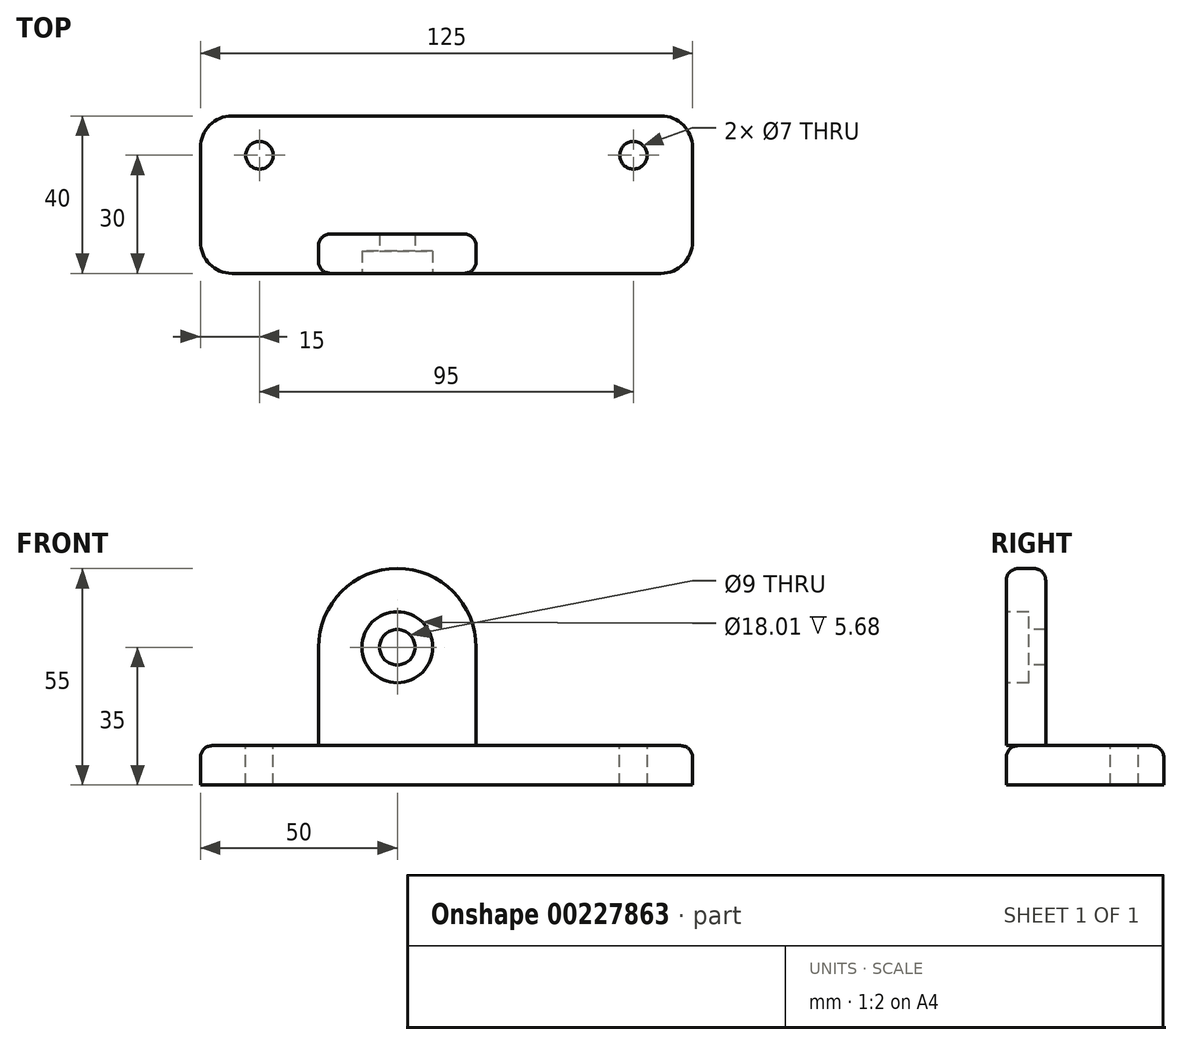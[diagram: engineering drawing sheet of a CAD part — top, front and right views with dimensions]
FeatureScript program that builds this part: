
annotation { "Feature Type Name" : "Feature", "Feature Type Description" : "" }
export const myFeature = defineFeature(function(context is Context, id is Id, definition is map)
    precondition{}
    {
        {
            var Q0;
            Q0=qCreatedBy(makeId("Top.planeOp"),FACE);
            var sketch = newSketch(context, id + "F0", { "sketchPlane" : qUnion([Q0])});
            skLineSegment(sketch, "E0.bottom", {"start": v(-62.5, 20) * mm, "end": v(62.5, 20) * mm});
            skLineSegment(sketch, "E0.top", {"start": v(-62.5, -20) * mm, "end": v(62.5, -20) * mm});
            skLineSegment(sketch, "E0.left", {"start": v(-62.5, 20) * mm, "end": v(-62.5, -20) * mm});
            skLineSegment(sketch, "E0.right", {"start": v(62.5, 20) * mm, "end": v(62.5, -20) * mm});
            skPoint(sketch, "E0.middle", {"position": v(0, 0) * mm});
            skSolve(sketch);
        }
        {
            var Q0;
            Q0=makeQuery(id+"F0.imprint","IMPRINT",FACE,{"disambiguationData":[TD([[makeQuery(id+"F0.imprint","IMPRINT",EDGE,{"derivedFrom":sQuery(id+"F0.wireOp",EDGE,"E0.bottom")}),-1.0]])]});
            extrude(context, id + "F1", {"entities" : qUnion([Q0]), "depth" : 10 * mm});
        }
        {
            var Q0;
            Q0=makeQuery(id+"F1.opExtrude","SWEPT_FACE",FACE,{"disambiguationData":[OSD([sQuery(id+"F0.wireOp",EDGE,"E0.top")])]});
            var sketch = newSketch(context, id + "F2", { "sketchPlane" : qUnion([Q0])});
            skLineSegment(sketch, "E1", {"start": v(-32.5, 10) * mm, "end": v(-32.5, 35) * mm});
            skLineSegment(sketch, "E2", {"start": v(7.5, 10) * mm, "end": v(7.5, 35) * mm});
            skArc(sketch, "E3", {"start": v(7.5, 35) * mm, "mid": v(-12.5, 55) * mm, "end": v(-32.5, 35) * mm});
            skSolve(sketch);
        }
        {
            var Q0;
            {var subQ0=sQuery(id+"F2.wireOp",EDGE,"E1");Q0=makeQuery(id+"F2.imprint","IMPRINT",FACE,{"disambiguationData":[TD([[makeQuery(id+"F2.imprint","IMPRINT",EDGE,{"derivedFrom":subQ0}),-1.0]])]});}
            extrude(context, id + "F3", {"entities" : qUnion([Q0]), "oppositeDirection" : true, "depth" : 10 * mm});
        }
        {
            var Q0;
            Q0=makeQuery(id+"F3.opExtrude","CAP_FACE",FACE,{"disambiguationData":[OSD([sQuery(id+"F0.wireOp",EDGE,"E0.top"),sQuery(id+"F2.wireOp",EDGE,"E1"),sQuery(id+"F2.wireOp",EDGE,"E2"),sQuery(id+"F2.wireOp",EDGE,"E3")])],"isStart":true});
            var sketch = newSketch(context, id + "F4", { "sketchPlane" : qUnion([Q0])});
            skPoint(sketch, "E4", {"position": v(-12.5, 35) * mm});
            skSolve(sketch);
        }
        {
            var Q0;
            Q0=sQuery(id+"F4.wireOp",VERTEX,"E4");
            var Q1;
            Q1=makeQuery(id+"F3.opExtrude","SWEPT_BODY",BODY,{"disambiguationData":[OSD([sQuery(id+"F0.wireOp",EDGE,"E0.top"),sQuery(id+"F2.wireOp",EDGE,"E1"),sQuery(id+"F2.wireOp",EDGE,"E2"),sQuery(id+"F2.wireOp",EDGE,"E3")])]});
            hole(context, id + "F5", {"style" : HoleStyle.C_BORE, "endStyle" : HoleEndStyle.THROUGH, "holeDiameter" : 9 * mm, "cBoreDiameter" : 18.01 * mm, "cBoreDepth" : 5.68 * mm, "locations" : qUnion([Q0]), "scope" : qUnion([Q1]), "isTappedThrough" : true});
        }
        {
            var Q0;
            Q0=makeQuery(id+"F1.opExtrude","CAP_FACE",FACE,{"disambiguationData":[OSD([sQuery(id+"F0.wireOp",EDGE,"E0.bottom"),sQuery(id+"F0.wireOp",EDGE,"E0.top"),sQuery(id+"F0.wireOp",EDGE,"E0.left"),sQuery(id+"F0.wireOp",EDGE,"E0.right")])],"isStart":false});
            var sketch = newSketch(context, id + "F6", { "sketchPlane" : qUnion([Q0])});
            skPoint(sketch, "E5", {"position": v(47.5, 10) * mm});
            skSolve(sketch);
        }
        {
            var Q0;
            Q0=sQuery(id+"F6.wireOp",VERTEX,"E5");
            var Q1;
            Q1=makeQuery(id+"F1.opExtrude","SWEPT_BODY",BODY,{"disambiguationData":[OSD([sQuery(id+"F0.wireOp",EDGE,"E0.bottom"),sQuery(id+"F0.wireOp",EDGE,"E0.top"),sQuery(id+"F0.wireOp",EDGE,"E0.left"),sQuery(id+"F0.wireOp",EDGE,"E0.right")])]});
            hole(context, id + "F7", {"style" : HoleStyle.SIMPLE, "endStyle" : HoleEndStyle.THROUGH, "holeDiameter" : 7 * mm, "locations" : qUnion([Q0]), "scope" : qUnion([Q1]), "isTappedThrough" : true});
        }
        {
            var Q0;
            Q0=makeQuery(id+"F1.opExtrude","CAP_FACE",FACE,{"disambiguationData":[OSD([sQuery(id+"F0.wireOp",EDGE,"E0.bottom"),sQuery(id+"F0.wireOp",EDGE,"E0.top"),sQuery(id+"F0.wireOp",EDGE,"E0.left"),sQuery(id+"F0.wireOp",EDGE,"E0.right")])],"isStart":false});
            var sketch = newSketch(context, id + "F8", { "sketchPlane" : qUnion([Q0])});
            skPoint(sketch, "E6", {"position": v(-47.5, 10) * mm});
            skSolve(sketch);
        }
        {
            var Q0;
            Q0=sQuery(id+"F8.wireOp",VERTEX,"E6");
            var Q1;
            Q1=makeQuery(id+"F1.opExtrude","SWEPT_BODY",BODY,{"disambiguationData":[OSD([sQuery(id+"F0.wireOp",EDGE,"E0.bottom"),sQuery(id+"F0.wireOp",EDGE,"E0.top"),sQuery(id+"F0.wireOp",EDGE,"E0.left"),sQuery(id+"F0.wireOp",EDGE,"E0.right")])]});
            hole(context, id + "F9", {"style" : HoleStyle.SIMPLE, "endStyle" : HoleEndStyle.THROUGH, "holeDiameter" : 7 * mm, "locations" : qUnion([Q0]), "scope" : qUnion([Q1]), "isTappedThrough" : true});
        }
        {
            var Q0;
            Q0=makeQuery(id+"F3.opExtrude","CAP_EDGE",EDGE,{"disambiguationData":[OSD([sQuery(id+"F2.wireOp",EDGE,"E3")])],"isStart":true});
            fillet(context, id + "F10", {"entities" : qUnion([Q0]), "radius" : 3 * mm, "tangentPropagation" : true, "allowEdgeOverflow" : false});
        }
        {
            var Q0;
            Q0=makeQuery(id+"F3.opExtrude","CAP_EDGE",EDGE,{"disambiguationData":[OSD([sQuery(id+"F2.wireOp",EDGE,"E3")])],"isStart":false});
            fillet(context, id + "F11", {"entities" : qUnion([Q0]), "radius" : 3 * mm, "tangentPropagation" : true, "allowEdgeOverflow" : false});
        }
        {
            var Q0;
            Q0=makeQuery(id+"F1.opExtrude","CAP_EDGE",EDGE,{"disambiguationData":[OSD([sQuery(id+"F0.wireOp",EDGE,"E0.left")])],"isStart":false});
            var Q1;
            Q1=makeQuery(id+"F1.opExtrude","CAP_EDGE",EDGE,{"disambiguationData":[OSD([sQuery(id+"F0.wireOp",EDGE,"E0.bottom")])],"isStart":false});
            var Q2;
            Q2=makeQuery(id+"F1.opExtrude","CAP_EDGE",EDGE,{"disambiguationData":[OSD([sQuery(id+"F0.wireOp",EDGE,"E0.right")])],"isStart":false});
            var Q3;
            Q3=makeQuery(id+"F1.opExtrude","CAP_EDGE",EDGE,{"disambiguationData":[OSD([sQuery(id+"F0.wireOp",EDGE,"E0.top")])],"isStart":false});
            fillet(context, id + "F12", {"entities" : qUnion([Q0, Q1, Q2, Q3]), "radius" : 3 * mm, "tangentPropagation" : true, "allowEdgeOverflow" : false});
        }
        {
            var Q0;
            Q0=makeQuery(id+"F1.opExtrude","SWEPT_EDGE",EDGE,{"disambiguationData":[OSD([sQuery(id+"F0.wireOp",EDGE,"E0.top"),sQuery(id+"F0.wireOp",EDGE,"E0.right")])]});
            var Q1;
            Q1=makeQuery(id+"F1.opExtrude","SWEPT_EDGE",EDGE,{"disambiguationData":[OSD([sQuery(id+"F0.wireOp",EDGE,"E0.bottom"),sQuery(id+"F0.wireOp",EDGE,"E0.right")])]});
            var Q2;
            Q2=makeQuery(id+"F1.opExtrude","SWEPT_EDGE",EDGE,{"disambiguationData":[OSD([sQuery(id+"F0.wireOp",EDGE,"E0.top"),sQuery(id+"F0.wireOp",EDGE,"E0.left")])]});
            var Q3;
            Q3=makeQuery(id+"F1.opExtrude","SWEPT_EDGE",EDGE,{"disambiguationData":[OSD([sQuery(id+"F0.wireOp",EDGE,"E0.bottom"),sQuery(id+"F0.wireOp",EDGE,"E0.left")])]});
            fillet(context, id + "F13", {"entities" : qUnion([Q0, Q1, Q2, Q3]), "radius" : 8 * mm, "tangentPropagation" : true, "allowEdgeOverflow" : false});
        }
    });
